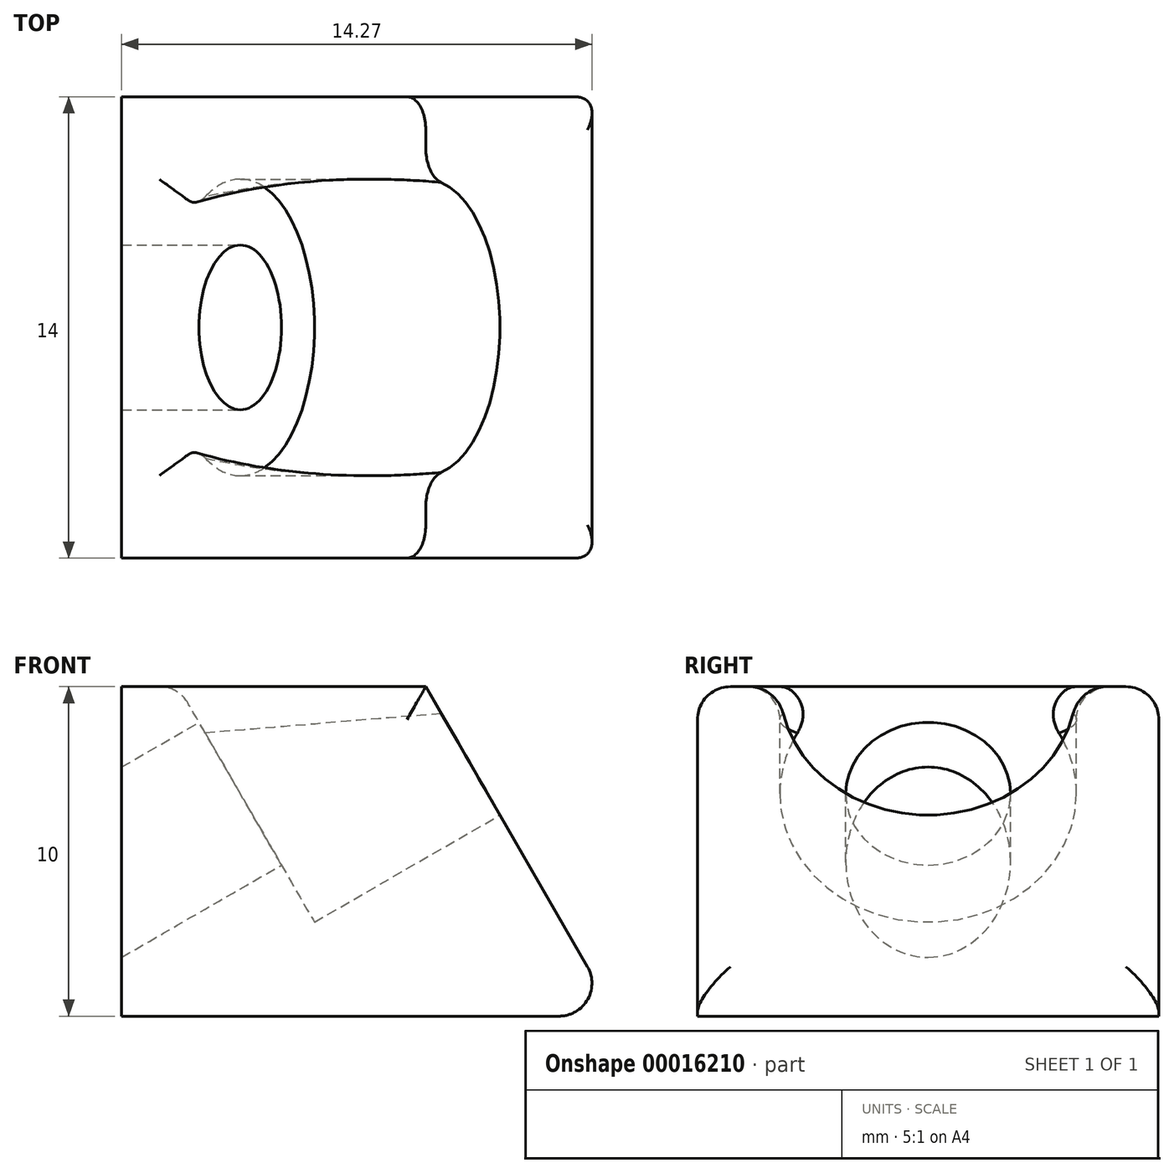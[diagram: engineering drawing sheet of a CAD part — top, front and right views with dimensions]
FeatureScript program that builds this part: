
annotation { "Feature Type Name" : "Feature", "Feature Type Description" : "" }
export const myFeature = defineFeature(function(context is Context, id is Id, definition is map)
    precondition{}
    {
        {
            var Q0;
            Q0=qCreatedBy(makeId("Top.planeOp"),FACE);
            var sketch = newSketch(context, id + "F0", { "sketchPlane" : qUnion([Q0])});
            skLineSegment(sketch, "E0.bottom", {"start": v(-9.23, 10) * mm, "end": v(5.77, 10) * mm});
            skLineSegment(sketch, "E0.top", {"start": v(-9.23, 0) * mm, "end": v(0, 0) * mm});
            skLineSegment(sketch, "E0.left", {"start": v(-9.23, 10) * mm, "end": v(-9.23, 0) * mm});
            skLineSegment(sketch, "E0.right", {"start": v(5.77, 10) * mm, "end": v(0, 0) * mm});
            skSolve(sketch);
        }
        {
            var Q0;
            Q0 = qSketchRegion(id + "F0", true);
            extrude(context, id + "F1", {"entities" : qUnion([Q0]), "endBound" : BoundingType.SYMMETRIC, "depth" : 14 * mm});
        }
        {
            var Q0;
            Q0=makeQuery(id+"F1.opExtrude","SWEPT_FACE",FACE,{"disambiguationData":[OSD([sQuery(id+"F0.wireOp",EDGE,"E0.right")])]});
            var sketch = newSketch(context, id + "F2", { "sketchPlane" : qUnion([Q0])});
            skLineSegment(sketch, "E1", {"start": v(11.55, 0) * mm, "end": v(0, 0) * mm, "construction": true});
            skCircle(sketch, "E2", {"center": v(0, 0) * mm, "radius": 4.5 * mm});
            skCircle(sketch, "E3", {"center": v(0, 0) * mm, "radius": 2.5 * mm});
            skSolve(sketch);
        }
        {
            var Q0;
            Q0=makeQuery(id+"F2.imprint","IMPRINT",FACE,{"disambiguationData":[TD([[makeQuery(id+"F2.imprint","IMPRINT",EDGE,{"derivedFrom":sQuery(id+"F2.wireOp",EDGE,"E3")}),-1.0]])]});
            extrude(context, id + "F3", {"entities" : qUnion([Q0]), "operationType" : NewBodyOperationType.REMOVE, "oppositeDirection" : true, "depth" : 6.5 * mm});
        }
        {
            var Q0;
            Q0=makeQuery(id+"F3.boolean.opBoolean","SPLIT",FACE,{"disambiguationData":[TD([makeQuery(id+"F3.opExtrude","SWEPT_FACE",FACE,{"disambiguationData":[OSD([sQuery(id+"F2.wireOp",EDGE,"E3")])]})])],"derivedFrom":makeQuery(id+"F1.opExtrude","SWEPT_FACE",FACE,{"disambiguationData":[OSD([sQuery(id+"F0.wireOp",EDGE,"E0.right")])]})});
            var Q1;
            Q1=makeQuery(id+"F3.boolean.opBoolean","SPLIT",FACE,{"disambiguationData":[TD([makeQuery(id+"F3.opExtrude","SWEPT_FACE",FACE,{"disambiguationData":[OSD([sQuery(id+"F2.wireOp",EDGE,"E3")])]})])],"derivedFrom":makeQuery(id+"F1.opExtrude","SWEPT_FACE",FACE,{"disambiguationData":[OSD([sQuery(id+"F0.wireOp",EDGE,"E0.top")])]})});
            extrude(context, id + "F4", {"entities" : qUnion([Q0, Q1]), "operationType" : NewBodyOperationType.REMOVE, "endBound" : BoundingType.THROUGH_ALL, "oppositeDirection" : true, "depth" : 25 * mm});
        }
        {
            var Q0;
            Q0=makeQuery(id+"F3.boolean.opBoolean","COPY",EDGE,{"derivedFrom":makeQuery(id+"F3.opExtrude","CAP_EDGE",EDGE,{"disambiguationData":[OSD([sQuery(id+"F2.wireOp",EDGE,"E2")])],"isStart":true})});
            var Q1;
            Q1=makeQuery(id+"F3.boolean.opBoolean","INTERSECT",EDGE,{"disambiguationData":[OD(1.0)],"derivedFrom":[makeQuery(id+"F1.opExtrude","SWEPT_FACE",FACE,{"disambiguationData":[OSD([sQuery(id+"F0.wireOp",EDGE,"E0.top")])]}),makeQuery(id+"F3.opExtrude","SWEPT_FACE",FACE,{"disambiguationData":[OSD([sQuery(id+"F2.wireOp",EDGE,"E2")])]})]});
            var Q2;
            Q2=makeQuery(id+"F3.boolean.opBoolean","INTERSECT",EDGE,{"disambiguationData":[OD(0.0)],"derivedFrom":[makeQuery(id+"F1.opExtrude","SWEPT_FACE",FACE,{"disambiguationData":[OSD([sQuery(id+"F0.wireOp",EDGE,"E0.top")])]}),makeQuery(id+"F3.opExtrude","SWEPT_FACE",FACE,{"disambiguationData":[OSD([sQuery(id+"F2.wireOp",EDGE,"E2")])]})]});
            var Q3;
            Q3=makeQuery(id+"F3.boolean.opBoolean","INTERSECT",EDGE,{"derivedFrom":[makeQuery(id+"F1.opExtrude","SWEPT_FACE",FACE,{"disambiguationData":[OSD([sQuery(id+"F0.wireOp",EDGE,"E0.top")])]}),makeQuery(id+"F3.opExtrude","CAP_FACE",FACE,{"disambiguationData":[OSD([sQuery(id+"F2.wireOp",EDGE,"E2"),sQuery(id+"F2.wireOp",EDGE,"E3")])],"isStart":false})]});
            fillet(context, id + "F5", {"entities" : qUnion([Q0, Q1, Q2, Q3]), "radius" : 1 * mm, "tangentPropagation" : true, "allowEdgeOverflow" : false});
        }
        {
            var Q0;
            Q0=makeQuery(id+"F1.opExtrude","CAP_EDGE",EDGE,{"disambiguationData":[OSD([sQuery(id+"F0.wireOp",EDGE,"E0.right")])],"isStart":false});
            var Q1;
            Q1=makeQuery(id+"F1.opExtrude","CAP_EDGE",EDGE,{"disambiguationData":[OSD([sQuery(id+"F0.wireOp",EDGE,"E0.top")])],"isStart":false});
            var Q2;
            Q2=makeQuery(id+"F1.opExtrude","CAP_EDGE",EDGE,{"disambiguationData":[OSD([sQuery(id+"F0.wireOp",EDGE,"E0.top")])],"isStart":true});
            var Q3;
            Q3=makeQuery(id+"F1.opExtrude","CAP_EDGE",EDGE,{"disambiguationData":[OSD([sQuery(id+"F0.wireOp",EDGE,"E0.right")])],"isStart":true});
            var Q4;
            Q4=makeQuery(id+"F1.opExtrude","SWEPT_EDGE",EDGE,{"disambiguationData":[OSD([sQuery(id+"F0.wireOp",EDGE,"E0.bottom"),sQuery(id+"F0.wireOp",EDGE,"E0.right")])]});
            fillet(context, id + "F6", {"entities" : qUnion([Q0, Q1, Q2, Q3, Q4]), "radius" : 1 * mm, "tangentPropagation" : true, "allowEdgeOverflow" : false});
        }
        {
            var Q0;
            Q0=makeQuery(id+"F1.opExtrude","SWEPT_BODY",BODY,{"disambiguationData":[OSD([sQuery(id+"F0.wireOp",EDGE,"E0.bottom"),sQuery(id+"F0.wireOp",EDGE,"E0.top"),sQuery(id+"F0.wireOp",EDGE,"E0.left"),sQuery(id+"F0.wireOp",EDGE,"E0.right")])]});
            var Q1;
            Q1=makeQuery(id+"F1.opExtrude","CAP_EDGE",EDGE,{"disambiguationData":[OSD([sQuery(id+"F0.wireOp",EDGE,"E0.bottom")])],"isStart":false});
            transform(context, id + "F7", {"entities" : qUnion([Q0]), "transformType" : TransformType.ROTATION, "transformAxis" : qUnion([Q1]), "angle" : 90 * degree, "oppositeDirection" : true, "makeCopy" : false});
        }
    });
